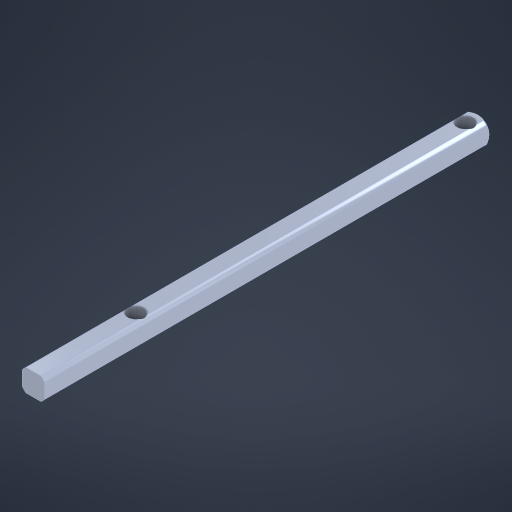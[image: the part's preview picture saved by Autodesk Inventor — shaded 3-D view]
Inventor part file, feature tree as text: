
AUTODESK INVENTOR PART (.ipt)
format: ipt  version: 2024 (Build 280153000, 153)  size: 310,784 bytes
history: native  units: in
note: dims shown in document units (in); Inventor stores cm internally (conversion verified against a paired STEP export)
features: other x50, sketch x3, extrude x2, thicken_offset x1, hole x1
ambient origin geometry x8: Origin, YZ Plane, XZ Plane, XY Plane, X Axis, Y Axis, Z Axis, Center Point
bodies: Solid1 (feature_tree)
feature tree (57):
  other  "Table"
  other  "Shaft HS 0.5 in"
  other  "Shaft HS 1.0 in"
  other  "Shaft HS 1.5 in"
  other  "Shaft HS 2.0 in"
  other  "Shaft HS 2.5 in"
  other  "Shaft HS 3.0 in"
  other  "Shaft HS 3.5 in"
  other  "Shaft HS 4.0 in"
  other  "Shaft HS 4.5 in"
  other  "Shaft HS 5.0 in"
  other  "Shaft HS 5.5 in"
  other  "Shaft HS 6.0 in"
  other  "Shaft HS 6.5 in"
  other  "Shaft HS 7.0 in"
  other  "Shaft HS 7.5 in"
  other  "Shaft HS 8.0 in"
  other  "Shaft HS 8.5 in"
  other  "Shaft HS 9.0 in"
  other  "Shaft HS 9.5 in"
  other  "Shaft HS 10.0 in"
  other  "Shaft HS 10.5 in"
  other  "Shaft HS 11.0 in"
  other  "Shaft HS 11.5 in"
  other  "Shaft HS 12.0 in"
  other  "Shaft HS 12.5 in"
  other  "Shaft HS 13.0 in"
  other  "Shaft HS 13.5 in"
  other  "Shaft HS 14.0 in"
  other  "Shaft HS 14.5 in"
  other  "Shaft HS 15.0 in"
  other  "Shaft HS 15.5 in"
  other  "Shaft HS 16.0 in"
  other  "Shaft HS 16.5 in"
  other  "Shaft HS 17.0 in"
  other  "Shaft HS 17.5 in"
  other  "Shaft HS 18.0 in"
  other  "Shaft HS 18.5 in"
  other  "Shaft HS 19.0 in"
  other  "Shaft HS 19.5 in"
  other  "Shaft HS 20.0 in"
  other  "Shaft HS 20.5 in"
  other  "Shaft HS 21.0 in"
  other  "Shaft HS 21.5 in"
  other  "Shaft HS 22.0 in"
  other  "Shaft HS 22.5 in"
  other  "Shaft HS 23.0 in"
  other  "Shaft HS 23.5 in"
  other  "Shaft HS 24.0 in"
  extrude  "Extrusion1"  Depth=12.1875in
  thicken_offset  "Thicken1"
  extrude  "Extrusion2"  Depth=19.125in
  hole  "Hole1"  [1 undecoded]
  sketch  "Sketch2"  dims[d0=0.0625in d1=0.0in d2=12.1875in]
  sketch  "Sketch3"  dims[d3=12.125in d4=19.125in]
  sketch  "Sketch6"  dims[d5=0.0in d9=0.15in d11=0.1875in d12=0.75in d13=0.375in d14=0.25in d15=0.5635in d16=1.0in d17=0.8108in d18=3.7in]
  other  "Cut-Revolve3"
note: 1 required parameter value undecoded (feature->parameter linkage not recoverable at this tier; creation-order binding heuristic only, values carry confidence <= 0.55)
